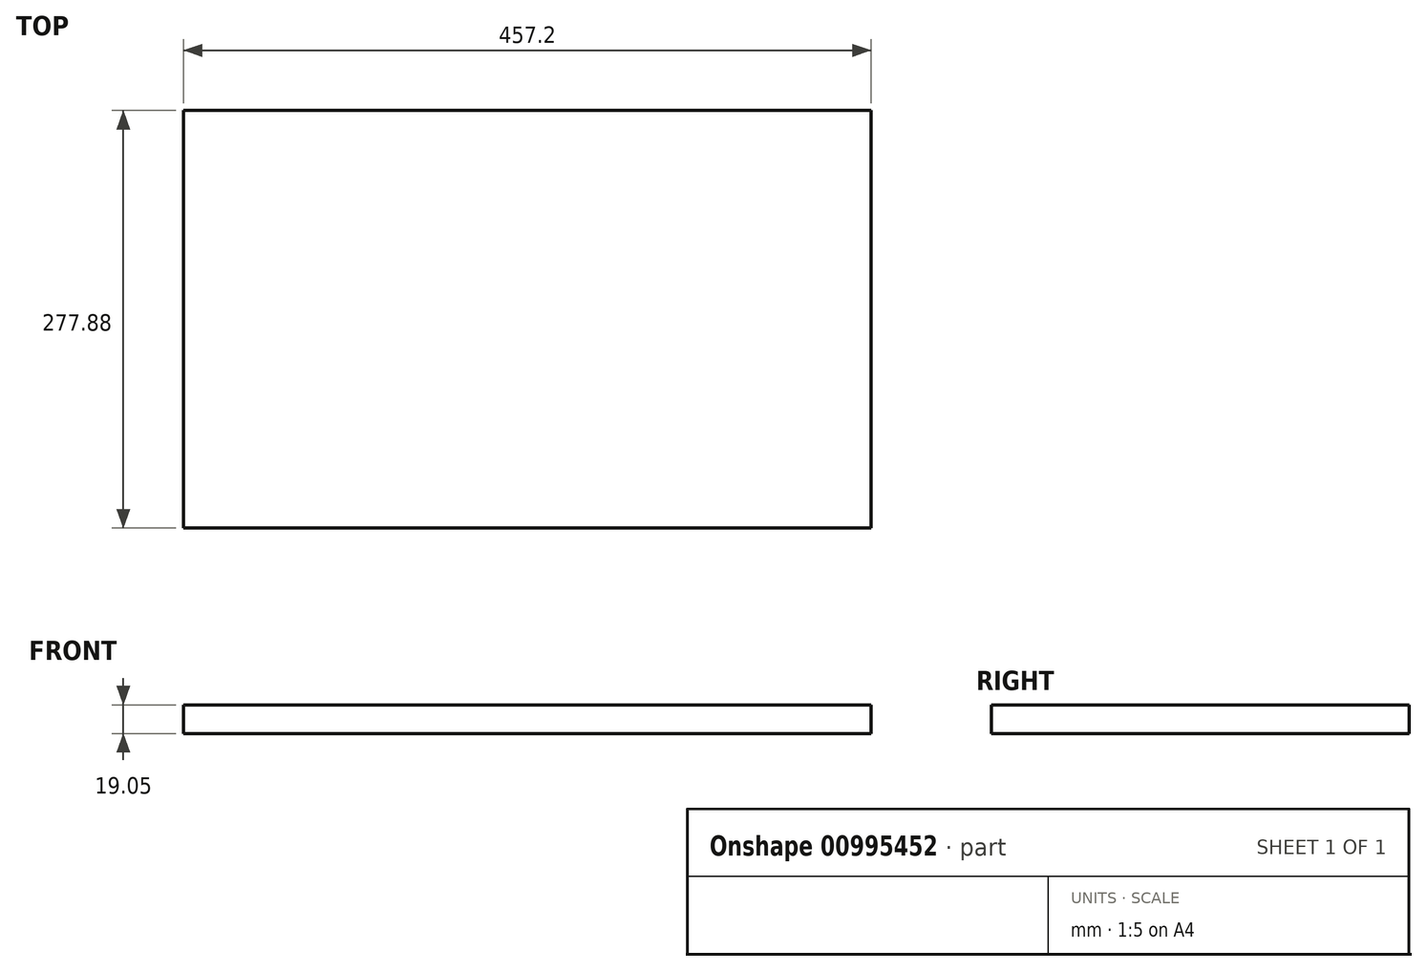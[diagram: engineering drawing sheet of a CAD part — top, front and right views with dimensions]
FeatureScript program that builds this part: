
annotation { "Feature Type Name" : "Feature", "Feature Type Description" : "" }
export const myFeature = defineFeature(function(context is Context, id is Id, definition is map)
    precondition{}
    {
        {
            var Q0;
            Q0=qCreatedBy(makeId("Front.planeOp"),FACE);
            var sketch = newSketch(context, id + "F0", { "sketchPlane" : qUnion([Q0])});
            skLineSegment(sketch, "E0.bottom", {"start": v(0, 0) * mm, "end": v(457.2, 0) * mm});
            skLineSegment(sketch, "E0.top", {"start": v(0, 19.05) * mm, "end": v(457.2, 19.05) * mm});
            skLineSegment(sketch, "E0.left", {"start": v(0, 0) * mm, "end": v(0, 19.05) * mm});
            skLineSegment(sketch, "E0.right", {"start": v(457.2, 0) * mm, "end": v(457.2, 19.05) * mm});
            skSolve(sketch);
        }
        {
            var Q0;
            Q0=makeQuery(id+"F0.imprint","IMPRINT",FACE,{"disambiguationData":[TD([[makeQuery(id+"F0.imprint","IMPRINT",EDGE,{"derivedFrom":sQuery(id+"F0.wireOp",EDGE,"E0.bottom")}),1.0]])]});
            extrude(context, id + "F1", {"entities" : qUnion([Q0]), "oppositeDirection" : true, "depth" : 277.88 * mm, "offsetDistance" : 25.4 * mm});
        }
    });
